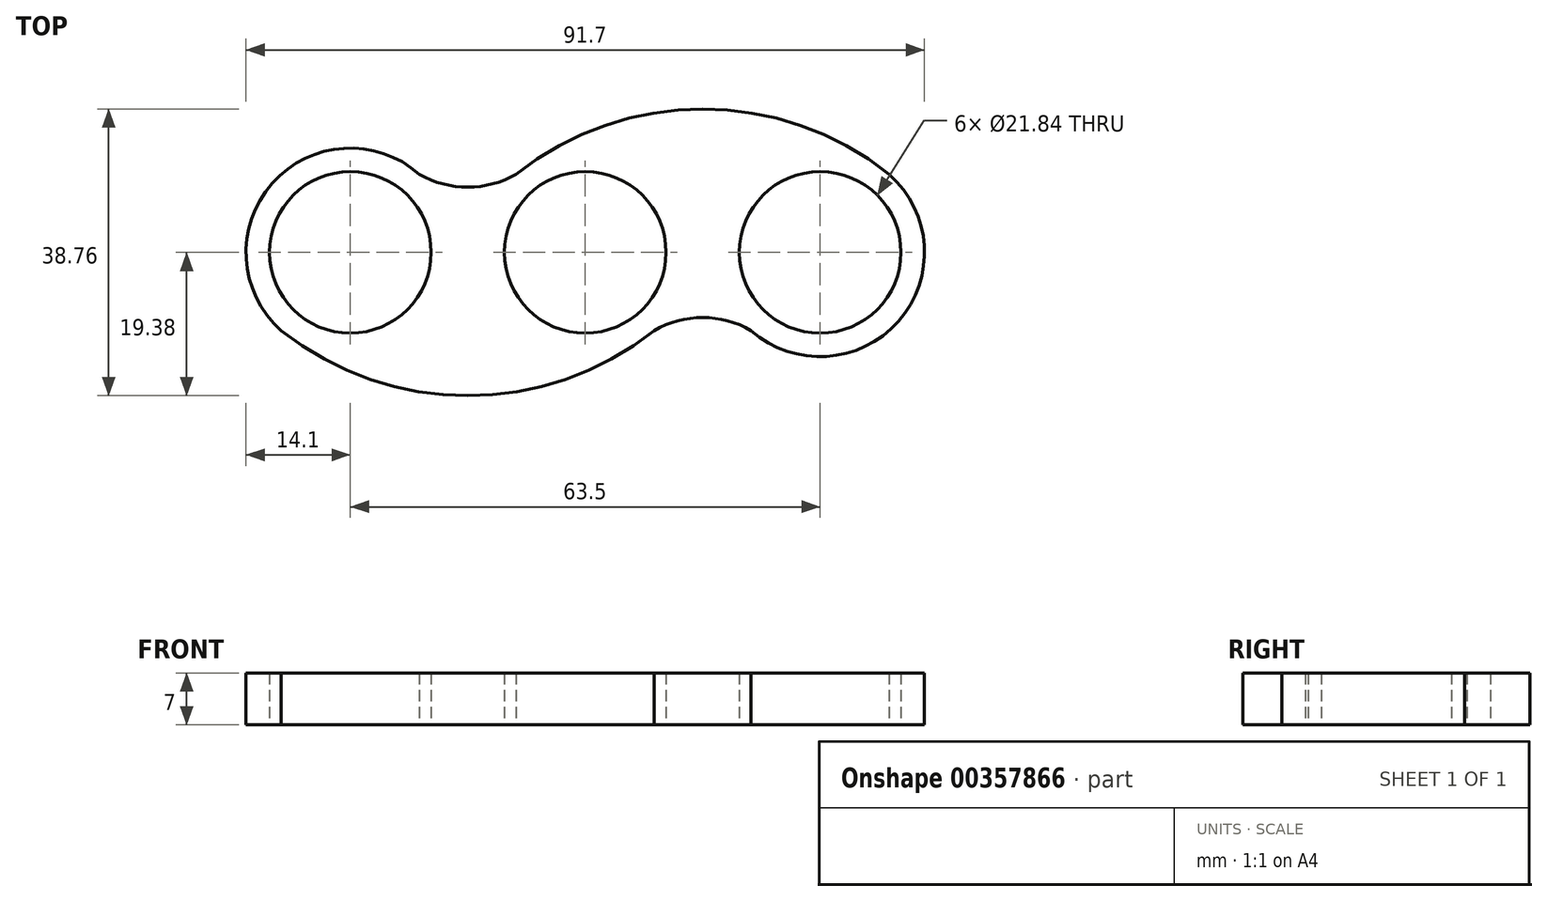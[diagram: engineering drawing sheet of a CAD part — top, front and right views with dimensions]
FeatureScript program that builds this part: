
annotation { "Feature Type Name" : "Feature", "Feature Type Description" : "" }
export const myFeature = defineFeature(function(context is Context, id is Id, definition is map)
    precondition{}
    {
        {
            var Q0;
            Q0=qCreatedBy(makeId("Top.planeOp"),FACE);
            var sketch = newSketch(context, id + "F0", { "sketchPlane" : qUnion([Q0])});
            skCircle(sketch, "E0", {"center": v(0, 0) * mm, "radius": 10.92 * mm});
            skCircle(sketch, "E1", {"center": v(0, 0) * mm, "radius": 14.1 * mm});
            skLineSegment(sketch, "E2", {"start": v(0, 0) * mm, "end": v(-31.75, 0) * mm});
            skLineSegment(sketch, "E3", {"start": v(0, 0) * mm, "end": v(31.75, 0) * mm});
            skCircle(sketch, "E4", {"center": v(31.75, 0) * mm, "radius": 10.92 * mm});
            skCircle(sketch, "E5", {"center": v(31.75, 0) * mm, "radius": 14.1 * mm});
            skCircle(sketch, "E6", {"center": v(-31.75, 0) * mm, "radius": 10.92 * mm});
            skCircle(sketch, "E7", {"center": v(-31.75, 0) * mm, "radius": 14.1 * mm});
            skPoint(sketch, "E8", {"position": v(-15.88, 0) * mm});
            skPoint(sketch, "E9", {"position": v(15.88, 0) * mm});
            skPoint(sketch, "E10", {"position": v(-15.88, 8.81) * mm});
            skPoint(sketch, "E11", {"position": v(15.88, -8.81) * mm});
            skPoint(sketch, "E12", {"position": v(-9.32, 10.57) * mm});
            skPoint(sketch, "E13", {"position": v(-22.42, 10.57) * mm});
            skArc(sketch, "E14", {"start": v(-22.42, 10.57) * mm, "mid": v(-15.87, 8.81) * mm, "end": v(-9.32, 10.57) * mm});
            skPoint(sketch, "E15", {"position": v(-41.08, -10.57) * mm});
            skPoint(sketch, "E16", {"position": v(9.33, -10.57) * mm});
            skPoint(sketch, "E17", {"position": v(41.08, 10.57) * mm});
            skPoint(sketch, "E18", {"position": v(22.42, -10.57) * mm});
            skArc(sketch, "E19", {"start": v(22.42, -10.57) * mm, "mid": v(15.88, -8.81) * mm, "end": v(9.33, -10.57) * mm});
            skPoint(sketch, "E20", {"position": v(-15.88, -19.38) * mm});
            skPoint(sketch, "E21", {"position": v(15.87, 19.38) * mm});
            skArc(sketch, "E22", {"start": v(-41.08, -10.57) * mm, "mid": v(-15.88, -19.38) * mm, "end": v(9.33, -10.57) * mm});
            skArc(sketch, "E23", {"start": v(41.08, 10.57) * mm, "mid": v(15.88, 19.38) * mm, "end": v(-9.32, 10.57) * mm});
            skSolve(sketch);
        }
        {
            var Q0;
            Q0=makeQuery(id+"F0.imprint","IMPRINT",FACE,{"disambiguationData":[TD([[makeQuery(id+"F0.imprint","IMPRINT",EDGE,{"derivedFrom":sQuery(id+"F0.wireOp",EDGE,"E6")}),-1.0]])]});
            var Q1;
            {var subQ0=sQuery(id+"F0.wireOp",EDGE,"E14");Q1=makeQuery(id+"F0.imprint","IMPRINT",FACE,{"disambiguationData":[TD([[makeQuery(id+"F0.imprint","IMPRINT",EDGE,{"derivedFrom":subQ0}),-1.0]])]});}
            var Q2;
            {var subQ0=sQuery(id+"F0.wireOp",EDGE,"E22");var subQ1=sQuery(id+"F0.wireOp",EDGE,"E1");var subQ2=makeQuery(id+"F0.imprint","INTERSECT",VERTEX,{"derivedFrom":[subQ1,subQ0]});Q2=makeQuery(id+"F0.imprint","IMPRINT",FACE,{"disambiguationData":[TD([[makeQuery(id+"F0.imprint","IMPRINT",EDGE,{"disambiguationData":[TD([[subQ2,1.0]])],"derivedFrom":subQ1}),-1.0]])]});}
            var Q3;
            {var subQ0=sQuery(id+"F0.wireOp",EDGE,"E2");var subQ1=sQuery(id+"F0.wireOp",EDGE,"E0");var subQ2=makeQuery(id+"F0.imprint","INTERSECT",VERTEX,{"derivedFrom":[subQ1,subQ0]});Q3=makeQuery(id+"F0.imprint","IMPRINT",FACE,{"disambiguationData":[TD([[makeQuery(id+"F0.imprint","IMPRINT",EDGE,{"disambiguationData":[TD([[subQ2,-1.0]])],"derivedFrom":subQ1}),-1.0]])]});}
            var Q4;
            {var subQ0=sQuery(id+"F0.wireOp",EDGE,"E2");var subQ1=sQuery(id+"F0.wireOp",EDGE,"E0");var subQ2=makeQuery(id+"F0.imprint","INTERSECT",VERTEX,{"derivedFrom":[subQ1,subQ0]});Q4=makeQuery(id+"F0.imprint","IMPRINT",FACE,{"disambiguationData":[TD([[makeQuery(id+"F0.imprint","IMPRINT",EDGE,{"disambiguationData":[TD([[subQ2,1.0]])],"derivedFrom":subQ1}),-1.0]])]});}
            var Q5;
            {var subQ0=sQuery(id+"F0.wireOp",EDGE,"E23");var subQ1=sQuery(id+"F0.wireOp",EDGE,"E1");var subQ2=makeQuery(id+"F0.imprint","INTERSECT",VERTEX,{"derivedFrom":[subQ1,subQ0]});Q5=makeQuery(id+"F0.imprint","IMPRINT",FACE,{"disambiguationData":[TD([[makeQuery(id+"F0.imprint","IMPRINT",EDGE,{"disambiguationData":[TD([[subQ2,1.0]])],"derivedFrom":subQ1}),-1.0]])]});}
            var Q6;
            {var subQ0=sQuery(id+"F0.wireOp",EDGE,"E19");Q6=makeQuery(id+"F0.imprint","IMPRINT",FACE,{"disambiguationData":[TD([[makeQuery(id+"F0.imprint","IMPRINT",EDGE,{"derivedFrom":subQ0}),-1.0]])]});}
            var Q7;
            Q7=makeQuery(id+"F0.imprint","IMPRINT",FACE,{"disambiguationData":[TD([[makeQuery(id+"F0.imprint","IMPRINT",EDGE,{"derivedFrom":sQuery(id+"F0.wireOp",EDGE,"E4")}),-1.0]])]});
            extrude(context, id + "F1", {"entities" : qUnion([Q0, Q1, Q2, Q3, Q4, Q5, Q6, Q7]), "depth" : 7 * mm});
        }
    });
